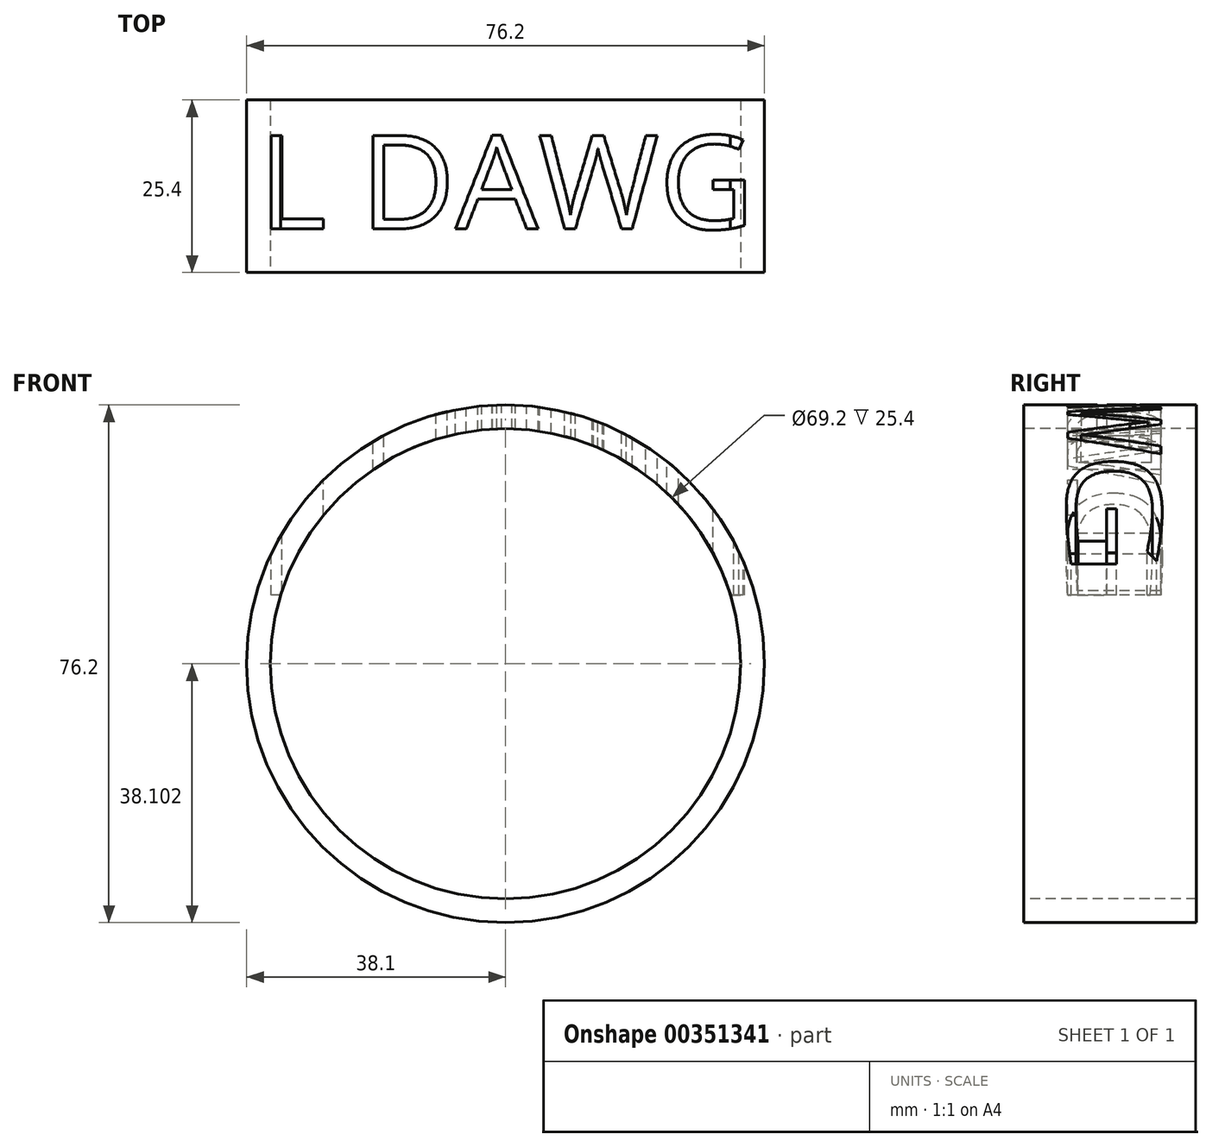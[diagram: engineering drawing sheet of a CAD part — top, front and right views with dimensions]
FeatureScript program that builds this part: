
annotation { "Feature Type Name" : "Feature", "Feature Type Description" : "" }
export const myFeature = defineFeature(function(context is Context, id is Id, definition is map)
    precondition{}
    {
        {
            var Q0;
            Q0=qCreatedBy(makeId("Front.planeOp"),FACE);
            var sketch = newSketch(context, id + "F0", { "sketchPlane" : qUnion([Q0])});
            skCircle(sketch, "E0", {"center": v(-4.73, 17.34) * mm, "radius": 38.1 * mm});
            skSolve(sketch);
        }
        {
            var Q0;
            Q0 = qSketchRegion(id + "F0", true);
            extrude(context, id + "F1", {"entities" : qUnion([Q0]), "depth" : 25.4 * mm});
        }
        {
            var Q0;
            Q0=makeQuery(id+"F1.opExtrude","CAP_FACE",FACE,{"disambiguationData":[OSD([sQuery(id+"F0.wireOp",EDGE,"E0")])],"isStart":false});
            var sketch = newSketch(context, id + "F2", { "sketchPlane" : qUnion([Q0])});
            skCircle(sketch, "E1", {"center": v(-4.73, 17.34) * mm, "radius": 34.6 * mm});
            skSolve(sketch);
        }
        {
            var Q0;
            Q0=makeQuery(id+"F2.imprint","IMPRINT",FACE,{"disambiguationData":[TD([[makeQuery(id+"F2.imprint","IMPRINT",EDGE,{"derivedFrom":sQuery(id+"F2.wireOp",EDGE,"E1")}),1.0]])]});
            extrude(context, id + "F3", {"entities" : qUnion([Q0]), "operationType" : NewBodyOperationType.REMOVE, "oppositeDirection" : true, "depth" : 25.4 * mm});
        }
        {
            var Q0;
            Q0=qCreatedBy(makeId("Top.planeOp"),FACE);
            cPlane(context, id + "F4", {"entities" : qUnion([Q0]), "cplaneType" : CPlaneType.OFFSET, "offset" : 65.53 * mm, "width" : 152.4 * mm, "height" : 152.4 * mm});
        }
        {
            var Q0;
            Q0=qCreatedBy(id+"F4.planeOp",FACE);
            var sketch = newSketch(context, id + "F5", { "sketchPlane" : qUnion([Q0])});
            skText(sketch, "E2", { "text": "L DAWG", "fontName": "OpenSans-Regular.ttf"});
            const initialGuessF5  = {"E2": [-0.0411, -0.01898, 1, 0, 0.01384]};
            skSetInitialGuess(sketch, initialGuessF5);
            skSolve(sketch);
        }
        {
            var Q0;
            Q0 = qSketchRegion(id + "F5", true);
            var Q1;
            Q1 = qConstructionFilter(qBodyType(qCreatedBy(id + "F5" ,EDGE), BodyType.WIRE), ConstructionObject.NO);
            extrude(context, id + "F6", {"entities" : qUnion([Q0]), "operationType" : NewBodyOperationType.REMOVE, "surfaceEntities" : qUnion([Q1]), "oppositeDirection" : true, "depth" : 38.1 * mm});
        }
    });
